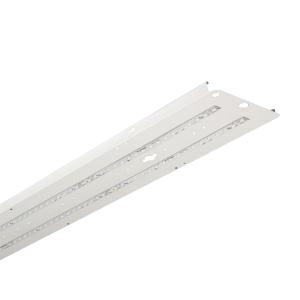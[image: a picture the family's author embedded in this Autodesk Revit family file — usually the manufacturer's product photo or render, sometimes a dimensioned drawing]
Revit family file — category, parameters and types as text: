
# Revit family: 3f_filippi_-_kit_led_retrofit_per_schermo_in_vetro_3f_filippi_-_a5118_-_kit_led_i3f_76__a3f_91__a3f_93_-_4ff908e0ef0cde77
name_source: partatom
category: Lighting Fixtures
units: mm (PartAtom-declared; Revit-internal decimal feet)

## family parameters
Cut with Voids When Loaded = No
Host = Face
Light Source = No
Part Type = Normal
Room Calculation Point = No
Round Connector Dimension = Use Diameter
Shared = No

## types (1)
- 3F Filippi - Kit LED Retrofit per schermo in vetro (1 x LED, 6938 lm, 49 W, 4000 K)
    Apparent Load = 49 VA
    Approval mark = ENEC
    CIE Flux Codes = 52 87 99 100 100
    Color Rendering = 80
    Color Temperature = 4000 K
    Control Gear = Electronic ballast
    Default Elevation = 1800 mm
    Description = Led retrofit kit suitable for Fluorescent Beta 2x i3F 76, A3F 91 and A3F 93 luminaires.

ILLUMINOTECHNICAL
Luminous efficiency 100% (DLOR 100%, ULOR 0%).
Initial luminous flux of the luminaire 6938 lm.
Symmetric distribution.
Installation Interdistance Transv.D = 1.29 x hu - Long.D = 1.29 x hu.
Tabular UGR (CIE 117 - 4H-8H; S=0.25H; 70/50/20): RUG 20.2 - 22.9.
Beam angle: 106° - 113°.
Luminous efficacy 142 lm/W.
Lifetime (L93/B10): 30000 h. (tq+25°C)
Lifetime (L90/B10): 50000 h. (tq+25°C)
Lifetime (L85/B10): 80000 h. (tq+25°C)
Lifetime (L80/B10): 100000 h. (tq+25°C)
Lifetime (L85/B10): 50000 h. (tq+35°C)
Sudden decreased luminous flux after 50000 hours: 0% (C0).
Photobiological safety in compliance with IEC/TR 62778: RG0 risk exempt, (IEC 62471).
In compliance with IEC/EN 62722-2-1 - IEC/EN 62717 standards.

SOURCE
2 linear LED modules 22W/840.
Energy efficiency class (UE 2019/2020 - UE 2019/2015): D.
CIE 13.3 Colour rendering index: CRI >80 (R9 <50%).
IES TM-30 Fidelity Index: Rf = 84 Rg = 95.
CCT nominal colour temperature 4000 K.
Colour initial tolerance (MacAdam): SDCM 3.

MECHANICAL
Gear-tray unit in hot-galvanised steel, painted in white polyester, fixed to the housing by means of "Ribloc" rapid devices in galvanised steel, hinged opening.
Luminaire with limited surface temperature. - D - (EN 60598-2-24)
Dimensions: 1565x235 mm, height 135 mm. Weight 1.75 kg.
Glow-wire test resistance 850°C.

ELECTRICAL
Halogen Free electronic wiring 230V-50/60Hz, power factor 0.97, THD <25%, constant output current, SELV, class I, 1 driver.
Power of the luminaire 49 W.
CE - IEC 60598-1 - EN 60598-1.
SAFE FLICKER: PstLM=<1 and SVM=<0.4 (IEC TR 61547-1 and IEC TR 63158), to ensure a more comfortable and safe light.
Luminaire compliant with EN 60598-2-22 for power supply from a centralised emergency system CPSS (Central Power Supply System), not incorporated in the luminaire - high risk areas excluded. The default power and flux are 100% in AC and 100% in DC.
Ambient temperature from -20°C to +35°C.
Temperature class T6 max 85°C.
Relative humidity UR: <85%.

INSTALLATION
Retrofit.
Correct installation of the retrofit LED kit, compliant with EN 60598-1 and CE marked, inside the 3F Filippi - Beta 2x i3F 76, A3F 91 and A3F 93 Fluorescent luminaires must be only carried out by qualified personnel to ensure compliance with the national installation standards.
Attention: to maintain the degree of protection of the device and for the purposes of validity of the guarantee of the new retrofit kits, it is imperative to replace the old cable guides (on the body of the device) with the new ones supplied.
All accessories dedicated to this product are available on the Catalog and on our website www.3F-Filippi.com.

WARNING
Fixture not suitable for cold stores with an ambient temperature <0°C and/or relative humidity >85%.
Luminaire designed for disposal/recycling at end-of-life.
Replaceable (LED only) light source by a professional. Replaceable control gear by a professional.
    Height = 135 mm
    Lamp = 1 x LED
    Lamp Light Flux = 6938 lm
    Lamp Power = 49 W
    Lamp count = 1
    Length = 1565 mm
    Lifetime = 50000 h
    Luminous efficacy = 142 lm/W
    Manufacturer = 3F Filippi
    ModVariant = No
    Model = 3F Filippi - A5118 - Kit LED I3F 76, A3F 91, A3F 93 - L1565-2X22W
    Mounting Place = Ceiling
    Mounting Type = Surface mounted
    Number of Poles = 1
    OnlyDefault = Yes
    Power Factor = 1
    Product Name = 3F Filippi - Kit LED Retrofit per schermo in vetro
    Product group = ceiling mounted luminaire
    ProductGroupID = 3
    Protection Class = Protection class I
    Protection Degree = Degree of protection
    RLX_Detail_Level = 1
    RLX_Emergency_Light_Flux = 0 lm
    RLX_Emergency_Type = 0
    RLX_Emergency_Type_DB = No
    RlxData = <blob elided: 53073 chars, md5=ecfca94b>
    Socket = socket
    Standby Power = 0 W
    System Light Flux = 6938 lm
    System Power = 49 W
    Type Comments = Product without accessories
    Type Image = 3ffilippi_a5118.jpg
    URL = http://relux.com
    VarID = ---
    Voltage = 0 V
    Weight = 0.00 kg
    Width = 235 mm

## geometry (parser evidence)
native form markers: Blend x4, Sweep x10
no freeform markers — native parametric forms only
